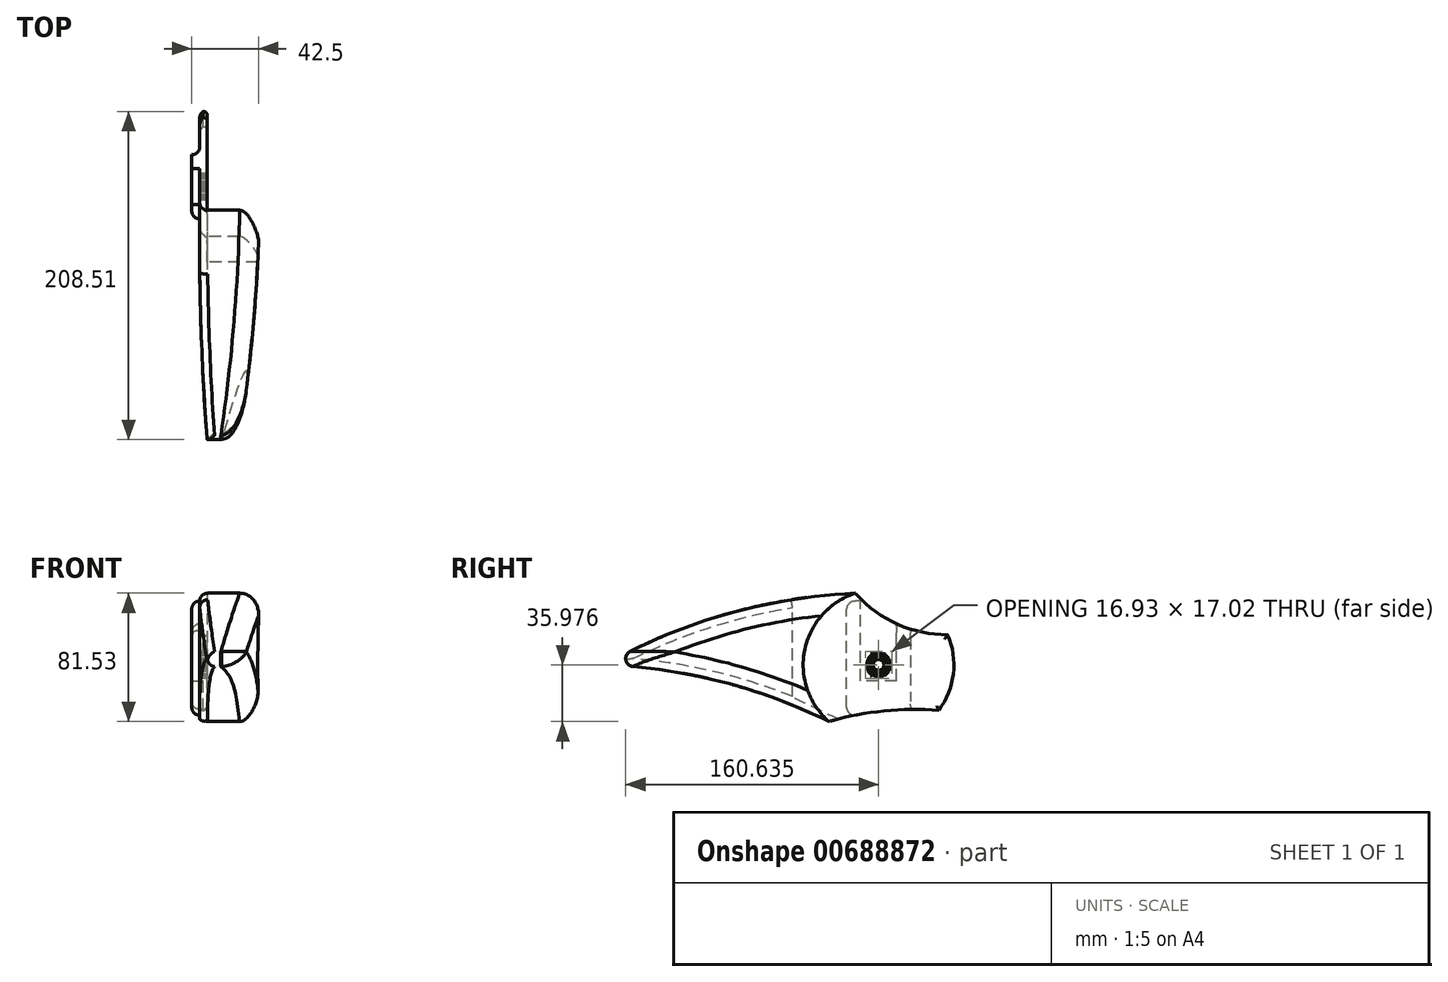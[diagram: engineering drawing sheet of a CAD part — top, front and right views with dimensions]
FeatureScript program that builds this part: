
annotation { "Feature Type Name" : "Feature", "Feature Type Description" : "" }
export const myFeature = defineFeature(function(context is Context, id is Id, definition is map)
    precondition{}
    {
        {
            var Q0;
            Q0=qCreatedBy(makeId("Right.planeOp"),FACE);
            var sketch = newSketch(context, id + "F0", { "sketchPlane" : qUnion([Q0])});
            skArc(sketch, "E0.0", {"start": v(-15.25, 45.51) * mm, "mid": v(-47.42, 9.65) * mm, "end": v(-32.12, -36.02) * mm});
            skArc(sketch, "E1", {"start": v(-15.25, 45.51) * mm, "mid": v(-97.5, 32.14) * mm, "end": v(-174.4, 0) * mm});
            skArc(sketch, "E2", {"start": v(-32.12, -36.02) * mm, "mid": v(-101.34, -10.43) * mm, "end": v(-174.4, 0) * mm});
            skArc(sketch, "E3", {"start": v(37.7, -28.86) * mm, "mid": v(2.47, -29.33) * mm, "end": v(-32.12, -36.02) * mm});
            skArc(sketch, "E4", {"start": v(-15.25, 45.51) * mm, "mid": v(11.16, 25.94) * mm, "end": v(43.33, 19.14) * mm});
            skArc(sketch, "E5.trimOffspring", {"start": v(37.7, -28.86) * mm, "mid": v(47.01, -5.62) * mm, "end": v(43.33, 19.14) * mm});
            skCircle(sketch, "E6", {"center": v(-0.54, -0.04) * mm, "radius": 3.43 * mm});
            skLineSegment(sketch, "E7", {"start": v(-0.54, -0.04) * mm, "end": v(-0.54, 10.9) * mm, "construction": true});
            skLineSegment(sketch, "E8.bottom", {"start": v(-0.55, 3.38) * mm, "end": v(-0.52, 3.38) * mm});
            skLineSegment(sketch, "E8.top", {"start": v(-0.55, 8.46) * mm, "end": v(-0.52, 8.46) * mm});
            skLineSegment(sketch, "E8.left", {"start": v(-0.55, 3.38) * mm, "end": v(-0.55, 8.46) * mm});
            skLineSegment(sketch, "E8.right", {"start": v(-0.52, 3.38) * mm, "end": v(-0.52, 8.46) * mm});
            skLineSegment(sketch, "E9.1.0", {"start": v(-1.24, 3.31) * mm, "end": v(-2.3, 8.28) * mm});
            skLineSegment(sketch, "E9.1.1", {"start": v(-1.26, 3.3) * mm, "end": v(-2.32, 8.28) * mm});
            skLineSegment(sketch, "E9.1.2", {"start": v(-2.32, 8.28) * mm, "end": v(-2.3, 8.28) * mm});
            skLineSegment(sketch, "E9.1.3", {"start": v(-1.26, 3.3) * mm, "end": v(-1.24, 3.31) * mm});
            skLineSegment(sketch, "E9.2.0", {"start": v(-1.92, 3.1) * mm, "end": v(-3.98, 7.73) * mm});
            skLineSegment(sketch, "E9.2.1", {"start": v(-1.94, 3.08) * mm, "end": v(-4, 7.72) * mm});
            skLineSegment(sketch, "E9.2.2", {"start": v(-4, 7.72) * mm, "end": v(-3.98, 7.73) * mm});
            skLineSegment(sketch, "E9.2.3", {"start": v(-1.94, 3.08) * mm, "end": v(-1.92, 3.1) * mm});
            skLineSegment(sketch, "E9.3.0", {"start": v(-2.54, 2.74) * mm, "end": v(-5.53, 6.85) * mm});
            skLineSegment(sketch, "E9.3.1", {"start": v(-2.56, 2.72) * mm, "end": v(-5.55, 6.83) * mm});
            skLineSegment(sketch, "E9.3.2", {"start": v(-5.55, 6.83) * mm, "end": v(-5.53, 6.85) * mm});
            skLineSegment(sketch, "E9.3.3", {"start": v(-2.56, 2.72) * mm, "end": v(-2.54, 2.74) * mm});
            skLineSegment(sketch, "E9.4.0", {"start": v(-3.08, 2.26) * mm, "end": v(-6.85, 5.66) * mm});
            skLineSegment(sketch, "E9.4.1", {"start": v(-3.1, 2.24) * mm, "end": v(-6.87, 5.64) * mm});
            skLineSegment(sketch, "E9.4.2", {"start": v(-6.87, 5.64) * mm, "end": v(-6.85, 5.66) * mm});
            skLineSegment(sketch, "E9.4.3", {"start": v(-3.1, 2.24) * mm, "end": v(-3.08, 2.26) * mm});
            skLineSegment(sketch, "E9.5.0", {"start": v(-3.5, 1.68) * mm, "end": v(-7.9, 4.22) * mm});
            skLineSegment(sketch, "E9.5.1", {"start": v(-3.51, 1.66) * mm, "end": v(-7.91, 4.2) * mm});
            skLineSegment(sketch, "E9.5.2", {"start": v(-7.91, 4.2) * mm, "end": v(-7.9, 4.22) * mm});
            skLineSegment(sketch, "E9.5.3", {"start": v(-3.51, 1.66) * mm, "end": v(-3.5, 1.68) * mm});
            skLineSegment(sketch, "E9.6.0", {"start": v(-3.8, 1.03) * mm, "end": v(-8.62, 2.6) * mm});
            skLineSegment(sketch, "E9.6.1", {"start": v(-3.8, 1) * mm, "end": v(-8.63, 2.57) * mm});
            skLineSegment(sketch, "E9.6.2", {"start": v(-8.63, 2.57) * mm, "end": v(-8.62, 2.6) * mm});
            skLineSegment(sketch, "E9.6.3", {"start": v(-3.8, 1) * mm, "end": v(-3.8, 1.03) * mm});
            skLineSegment(sketch, "E9.7.0", {"start": v(-3.94, 0.33) * mm, "end": v(-9, 0.86) * mm});
            skLineSegment(sketch, "E9.7.1", {"start": v(-3.95, 0.3) * mm, "end": v(-9, 0.83) * mm});
            skLineSegment(sketch, "E9.7.2", {"start": v(-9, 0.83) * mm, "end": v(-9, 0.86) * mm});
            skLineSegment(sketch, "E9.7.3", {"start": v(-3.95, 0.3) * mm, "end": v(-3.94, 0.33) * mm});
            skLineSegment(sketch, "E9.8.0", {"start": v(-3.95, -0.39) * mm, "end": v(-9, -0.92) * mm});
            skLineSegment(sketch, "E9.8.1", {"start": v(-3.94, -0.42) * mm, "end": v(-9, -0.95) * mm});
            skLineSegment(sketch, "E9.8.2", {"start": v(-9, -0.95) * mm, "end": v(-9, -0.92) * mm});
            skLineSegment(sketch, "E9.8.3", {"start": v(-3.94, -0.42) * mm, "end": v(-3.95, -0.39) * mm});
            skLineSegment(sketch, "E9.9.0", {"start": v(-3.8, -1.1) * mm, "end": v(-8.63, -2.66) * mm});
            skLineSegment(sketch, "E9.9.1", {"start": v(-3.8, -1.12) * mm, "end": v(-8.62, -2.69) * mm});
            skLineSegment(sketch, "E9.9.2", {"start": v(-8.62, -2.69) * mm, "end": v(-8.63, -2.66) * mm});
            skLineSegment(sketch, "E9.9.3", {"start": v(-3.8, -1.12) * mm, "end": v(-3.8, -1.1) * mm});
            skLineSegment(sketch, "E10.3.10.0", {"start": v(-3.5, -1.77) * mm, "end": v(-7.9, -4.3) * mm});
            skLineSegment(sketch, "E10.4.10.0", {"start": v(-3.51, -1.75) * mm, "end": v(-7.91, -4.29) * mm});
            skLineSegment(sketch, "E10.6.10.0", {"start": v(-7.9, -4.3) * mm, "end": v(-7.91, -4.29) * mm});
            skLineSegment(sketch, "E10.9.10.0", {"start": v(-3.5, -1.77) * mm, "end": v(-3.51, -1.75) * mm});
            skLineSegment(sketch, "E11.3.11.0", {"start": v(-3.08, -2.35) * mm, "end": v(-6.85, -5.75) * mm});
            skLineSegment(sketch, "E11.4.11.0", {"start": v(-3.1, -2.33) * mm, "end": v(-6.87, -5.73) * mm});
            skLineSegment(sketch, "E11.6.11.0", {"start": v(-6.85, -5.75) * mm, "end": v(-6.87, -5.73) * mm});
            skLineSegment(sketch, "E11.9.11.0", {"start": v(-3.08, -2.35) * mm, "end": v(-3.1, -2.33) * mm});
            skLineSegment(sketch, "E12.3.12.0", {"start": v(-2.54, -2.83) * mm, "end": v(-5.53, -6.94) * mm});
            skLineSegment(sketch, "E12.4.12.0", {"start": v(-2.56, -2.81) * mm, "end": v(-5.55, -6.92) * mm});
            skLineSegment(sketch, "E12.6.12.0", {"start": v(-5.53, -6.94) * mm, "end": v(-5.55, -6.92) * mm});
            skLineSegment(sketch, "E12.9.12.0", {"start": v(-2.54, -2.83) * mm, "end": v(-2.56, -2.81) * mm});
            skLineSegment(sketch, "E13.3.13.0", {"start": v(-1.92, -3.18) * mm, "end": v(-3.98, -7.82) * mm});
            skLineSegment(sketch, "E13.4.13.0", {"start": v(-1.94, -3.17) * mm, "end": v(-4, -7.81) * mm});
            skLineSegment(sketch, "E13.6.13.0", {"start": v(-3.98, -7.82) * mm, "end": v(-4, -7.81) * mm});
            skLineSegment(sketch, "E13.9.13.0", {"start": v(-1.92, -3.18) * mm, "end": v(-1.94, -3.17) * mm});
            skLineSegment(sketch, "E13.3.14.0", {"start": v(-1.24, -3.4) * mm, "end": v(-2.3, -8.37) * mm});
            skLineSegment(sketch, "E13.4.14.0", {"start": v(-1.26, -3.4) * mm, "end": v(-2.32, -8.36) * mm});
            skLineSegment(sketch, "E13.6.14.0", {"start": v(-2.3, -8.37) * mm, "end": v(-2.32, -8.36) * mm});
            skLineSegment(sketch, "E13.9.14.0", {"start": v(-1.24, -3.4) * mm, "end": v(-1.26, -3.4) * mm});
            skLineSegment(sketch, "E14.3.15.0", {"start": v(-0.52, -3.47) * mm, "end": v(-0.52, -8.55) * mm});
            skLineSegment(sketch, "E14.4.15.0", {"start": v(-0.55, -3.47) * mm, "end": v(-0.55, -8.55) * mm});
            skLineSegment(sketch, "E14.6.15.0", {"start": v(-0.52, -8.55) * mm, "end": v(-0.55, -8.55) * mm});
            skLineSegment(sketch, "E14.9.15.0", {"start": v(-0.52, -3.47) * mm, "end": v(-0.55, -3.47) * mm});
            skLineSegment(sketch, "E14.3.16.0", {"start": v(0.2, -3.4) * mm, "end": v(1.25, -8.36) * mm});
            skLineSegment(sketch, "E14.4.16.0", {"start": v(0.17, -3.4) * mm, "end": v(1.22, -8.37) * mm});
            skLineSegment(sketch, "E14.6.16.0", {"start": v(1.25, -8.36) * mm, "end": v(1.22, -8.37) * mm});
            skLineSegment(sketch, "E14.9.16.0", {"start": v(0.2, -3.4) * mm, "end": v(0.17, -3.4) * mm});
            skLineSegment(sketch, "E14.3.17.0", {"start": v(0.87, -3.17) * mm, "end": v(2.94, -7.81) * mm});
            skLineSegment(sketch, "E14.4.17.0", {"start": v(0.85, -3.18) * mm, "end": v(2.91, -7.82) * mm});
            skLineSegment(sketch, "E14.6.17.0", {"start": v(2.94, -7.81) * mm, "end": v(2.91, -7.82) * mm});
            skLineSegment(sketch, "E14.9.17.0", {"start": v(0.87, -3.17) * mm, "end": v(0.85, -3.18) * mm});
            skLineSegment(sketch, "E14.3.18.0", {"start": v(1.5, -2.81) * mm, "end": v(4.48, -6.92) * mm});
            skLineSegment(sketch, "E14.4.18.0", {"start": v(1.47, -2.83) * mm, "end": v(4.46, -6.94) * mm});
            skLineSegment(sketch, "E14.6.18.0", {"start": v(4.48, -6.92) * mm, "end": v(4.46, -6.94) * mm});
            skLineSegment(sketch, "E14.9.18.0", {"start": v(1.5, -2.81) * mm, "end": v(1.47, -2.83) * mm});
            skLineSegment(sketch, "E14.3.19.0", {"start": v(2.02, -2.33) * mm, "end": v(5.8, -5.73) * mm});
            skLineSegment(sketch, "E14.4.19.0", {"start": v(2, -2.35) * mm, "end": v(5.78, -5.75) * mm});
            skLineSegment(sketch, "E14.6.19.0", {"start": v(5.8, -5.73) * mm, "end": v(5.78, -5.75) * mm});
            skLineSegment(sketch, "E14.9.19.0", {"start": v(2.02, -2.33) * mm, "end": v(2, -2.35) * mm});
            skLineSegment(sketch, "E15.3.20.0", {"start": v(2.44, -1.75) * mm, "end": v(6.84, -4.29) * mm});
            skLineSegment(sketch, "E15.4.20.0", {"start": v(2.43, -1.77) * mm, "end": v(6.83, -4.3) * mm});
            skLineSegment(sketch, "E15.6.20.0", {"start": v(6.84, -4.29) * mm, "end": v(6.83, -4.3) * mm});
            skLineSegment(sketch, "E15.9.20.0", {"start": v(2.44, -1.75) * mm, "end": v(2.43, -1.77) * mm});
            skLineSegment(sketch, "E15.3.21.0", {"start": v(2.73, -1.1) * mm, "end": v(7.56, -2.66) * mm});
            skLineSegment(sketch, "E15.4.21.0", {"start": v(2.72, -1.12) * mm, "end": v(7.55, -2.69) * mm});
            skLineSegment(sketch, "E15.6.21.0", {"start": v(7.56, -2.66) * mm, "end": v(7.55, -2.69) * mm});
            skLineSegment(sketch, "E15.9.21.0", {"start": v(2.73, -1.1) * mm, "end": v(2.72, -1.12) * mm});
            skLineSegment(sketch, "E15.3.22.0", {"start": v(2.88, -0.39) * mm, "end": v(7.93, -0.92) * mm});
            skLineSegment(sketch, "E15.4.22.0", {"start": v(2.87, -0.42) * mm, "end": v(7.93, -0.95) * mm});
            skLineSegment(sketch, "E15.6.22.0", {"start": v(7.93, -0.92) * mm, "end": v(7.93, -0.95) * mm});
            skLineSegment(sketch, "E15.9.22.0", {"start": v(2.88, -0.39) * mm, "end": v(2.87, -0.42) * mm});
            skLineSegment(sketch, "E15.3.23.0", {"start": v(2.87, 0.33) * mm, "end": v(7.93, 0.86) * mm});
            skLineSegment(sketch, "E15.4.23.0", {"start": v(2.88, 0.3) * mm, "end": v(7.93, 0.83) * mm});
            skLineSegment(sketch, "E15.6.23.0", {"start": v(7.93, 0.86) * mm, "end": v(7.93, 0.83) * mm});
            skLineSegment(sketch, "E15.9.23.0", {"start": v(2.87, 0.33) * mm, "end": v(2.88, 0.3) * mm});
            skLineSegment(sketch, "E15.3.24.0", {"start": v(2.72, 1.03) * mm, "end": v(7.55, 2.6) * mm});
            skLineSegment(sketch, "E15.4.24.0", {"start": v(2.73, 1) * mm, "end": v(7.56, 2.57) * mm});
            skLineSegment(sketch, "E15.6.24.0", {"start": v(7.55, 2.6) * mm, "end": v(7.56, 2.57) * mm});
            skLineSegment(sketch, "E15.9.24.0", {"start": v(2.72, 1.03) * mm, "end": v(2.73, 1) * mm});
            skLineSegment(sketch, "E16.3.25.0", {"start": v(2.43, 1.68) * mm, "end": v(6.83, 4.22) * mm});
            skLineSegment(sketch, "E16.4.25.0", {"start": v(2.44, 1.66) * mm, "end": v(6.84, 4.2) * mm});
            skLineSegment(sketch, "E16.6.25.0", {"start": v(6.83, 4.22) * mm, "end": v(6.84, 4.2) * mm});
            skLineSegment(sketch, "E16.9.25.0", {"start": v(2.43, 1.68) * mm, "end": v(2.44, 1.66) * mm});
            skLineSegment(sketch, "E16.3.26.0", {"start": v(2, 2.26) * mm, "end": v(5.78, 5.66) * mm});
            skLineSegment(sketch, "E16.4.26.0", {"start": v(2.02, 2.24) * mm, "end": v(5.8, 5.64) * mm});
            skLineSegment(sketch, "E16.6.26.0", {"start": v(5.78, 5.66) * mm, "end": v(5.8, 5.64) * mm});
            skLineSegment(sketch, "E16.9.26.0", {"start": v(2, 2.26) * mm, "end": v(2.02, 2.24) * mm});
            skLineSegment(sketch, "E16.3.27.0", {"start": v(1.47, 2.74) * mm, "end": v(4.46, 6.85) * mm});
            skLineSegment(sketch, "E16.4.27.0", {"start": v(1.5, 2.72) * mm, "end": v(4.48, 6.83) * mm});
            skLineSegment(sketch, "E16.6.27.0", {"start": v(4.46, 6.85) * mm, "end": v(4.48, 6.83) * mm});
            skLineSegment(sketch, "E16.9.27.0", {"start": v(1.47, 2.74) * mm, "end": v(1.5, 2.72) * mm});
            skLineSegment(sketch, "E16.3.28.0", {"start": v(0.85, 3.1) * mm, "end": v(2.91, 7.73) * mm});
            skLineSegment(sketch, "E16.4.28.0", {"start": v(0.87, 3.08) * mm, "end": v(2.94, 7.72) * mm});
            skLineSegment(sketch, "E16.6.28.0", {"start": v(2.91, 7.73) * mm, "end": v(2.94, 7.72) * mm});
            skLineSegment(sketch, "E16.9.28.0", {"start": v(0.85, 3.1) * mm, "end": v(0.87, 3.08) * mm});
            skLineSegment(sketch, "E16.3.29.0", {"start": v(0.17, 3.31) * mm, "end": v(1.22, 8.28) * mm});
            skLineSegment(sketch, "E16.4.29.0", {"start": v(0.2, 3.3) * mm, "end": v(1.25, 8.28) * mm});
            skLineSegment(sketch, "E16.6.29.0", {"start": v(1.22, 8.28) * mm, "end": v(1.25, 8.28) * mm});
            skLineSegment(sketch, "E16.9.29.0", {"start": v(0.17, 3.31) * mm, "end": v(0.2, 3.3) * mm});
            skSolve(sketch);
        }
        {
            var Q0;
            Q0=makeQuery(id+"F0.imprint","IMPRINT",FACE,{"disambiguationData":[TD([[makeQuery(id+"F0.imprint","IMPRINT",EDGE,{"derivedFrom":sQuery(id+"F0.wireOp",EDGE,"E0.0")}),1.0]])]});
            extrude(context, id + "F1", {"entities" : qUnion([Q0]), "depth" : 4.83 * mm, "offsetDistance" : 25.4 * mm});
        }
        {
            var Q0;
            Q0=makeQuery(id+"F0.imprint","IMPRINT",FACE,{"disambiguationData":[TD([[makeQuery(id+"F0.imprint","IMPRINT",EDGE,{"derivedFrom":sQuery(id+"F0.wireOp",EDGE,"E0.0")}),-1.0]])]});
            extrude(context, id + "F2", {"entities" : qUnion([Q0]), "operationType" : NewBodyOperationType.ADD, "depth" : 38.1 * mm, "offsetDistance" : 25.4 * mm});
        }
        {
            var Q0;
            Q0=makeQuery(id+"F1.opExtrude","CAP_EDGE",EDGE,{"disambiguationData":[OSD([sQuery(id+"F0.wireOp",EDGE,"E4")])],"isStart":false});
            var Q1;
            Q1=makeQuery(id+"F1.opExtrude","CAP_EDGE",EDGE,{"disambiguationData":[OSD([sQuery(id+"F0.wireOp",EDGE,"E3")])],"isStart":false});
            var Q2;
            Q2=makeQuery(id+"F1.opExtrude","CAP_EDGE",EDGE,{"disambiguationData":[OSD([sQuery(id+"F0.wireOp",EDGE,"E5.trimOffspring")])],"isStart":false});
            fillet(context, id + "F3", {"entities" : qUnion([Q0, Q1, Q2]), "radius" : 2.54 * mm, "tangentPropagation" : true, "allowEdgeOverflow" : false});
        }
        {
            var Q0;
            Q0=makeQuery(id+"F2.boolean.opBoolean","SPLIT",EDGE,{"derivedFrom":makeQuery(id+"F2.opExtrude","SWEPT_EDGE",EDGE,{"disambiguationData":[OSD([sQuery(id+"F0.wireOp",EDGE,"E0.0"),sQuery(id+"F0.wireOp",EDGE,"E1"),sQuery(id+"F0.wireOp",EDGE,"E4")])]})});
            cPlane(context, id + "F4", {"entities" : qUnion([Q0]), "cplaneType" : CPlaneType.LINE_ANGLE, "offset" : 0 * mm, "angle" : 90 * degree, "width" : 152.4 * mm, "height" : 152.4 * mm});
        }
        {
            var Q0;
            Q0=qCreatedBy(id+"F4.planeOp",FACE);
            var sketch = newSketch(context, id + "F5", { "sketchPlane" : qUnion([Q0])});
            skLineSegment(sketch, "E17", {"start": v(22.21, -178.45) * mm, "end": v(43.85, -178.45) * mm});
            skLineSegment(sketch, "E18", {"start": v(43.85, -178.45) * mm, "end": v(43.85, -15.25) * mm});
            skLineSegment(sketch, "E19", {"start": v(43.85, -15.25) * mm, "end": v(38.1, -15.25) * mm});
            skArc(sketch, "E20", {"start": v(22.21, -178.45) * mm, "mid": v(33.2, -97.15) * mm, "end": v(38.1, -15.25) * mm});
            skArc(sketch, "E21", {"start": v(0, -15.25) * mm, "mid": v(0.95, -94.53) * mm, "end": v(5.71, -173.68) * mm});
            skLineSegment(sketch, "E22", {"start": v(0, -15.25) * mm, "end": v(-6.93, -15.25) * mm});
            skLineSegment(sketch, "E23", {"start": v(-6.93, -15.25) * mm, "end": v(-6.93, -180.22) * mm});
            skLineSegment(sketch, "E24", {"start": v(-6.93, -180.22) * mm, "end": v(5.71, -180.22) * mm});
            skLineSegment(sketch, "E25", {"start": v(5.71, -180.22) * mm, "end": v(5.71, -173.68) * mm});
            skSolve(sketch);
        }
        {
            var Q0;
            Q0 = qSketchRegion(id + "F5", true);
            extrude(context, id + "F6", {"entities" : qUnion([Q0]), "operationType" : NewBodyOperationType.REMOVE, "endBound" : BoundingType.THROUGH_ALL, "oppositeDirection" : true, "depth" : 25.4 * mm, "offsetDistance" : 25.4 * mm});
        }
        {
            var Q0;
            Q0=makeQuery(id+"F6.boolean.opBoolean","INTERSECT",EDGE,{"derivedFrom":[makeQuery(id+"F2.opExtrude","SWEPT_FACE",FACE,{"disambiguationData":[OSD([sQuery(id+"F0.wireOp",EDGE,"E1")])]}),makeQuery(id+"F6.opExtrude","SWEPT_FACE",FACE,{"disambiguationData":[OSD([sQuery(id+"F5.wireOp",EDGE,"E20")])]})]});
            var Q1;
            Q1=makeQuery(id+"F6.boolean.opBoolean","INTERSECT",EDGE,{"derivedFrom":[makeQuery(id+"F2.opExtrude","SWEPT_FACE",FACE,{"disambiguationData":[OSD([sQuery(id+"F0.wireOp",EDGE,"E2")])]}),makeQuery(id+"F6.opExtrude","SWEPT_FACE",FACE,{"disambiguationData":[OSD([sQuery(id+"F5.wireOp",EDGE,"E20")])]})]});
            fillet(context, id + "F7", {"entities" : qUnion([Q0, Q1]), "radius" : 12.7 * mm, "tangentPropagation" : true, "allowEdgeOverflow" : false});
        }
        {
            var Q0;
            Q0=makeQuery(id+"F2.opExtrude","SWEPT_EDGE",EDGE,{"disambiguationData":[OSD([sQuery(id+"F0.wireOp",EDGE,"E1"),sQuery(id+"F0.wireOp",EDGE,"E2")])]});
            var Q1;
            Q1=makeQuery(id+"F6.boolean.opBoolean","INTERSECT",EDGE,{"derivedFrom":[makeQuery(id+"F2.opExtrude","SWEPT_FACE",FACE,{"disambiguationData":[OSD([sQuery(id+"F0.wireOp",EDGE,"E1")])]}),makeQuery(id+"F6.opExtrude","SWEPT_FACE",FACE,{"disambiguationData":[OSD([sQuery(id+"F5.wireOp",EDGE,"E21")])]})]});
            var Q2;
            Q2=makeQuery(id+"F6.boolean.opBoolean","INTERSECT",EDGE,{"derivedFrom":[makeQuery(id+"F2.opExtrude","SWEPT_FACE",FACE,{"disambiguationData":[OSD([sQuery(id+"F0.wireOp",EDGE,"E2")])]}),makeQuery(id+"F6.opExtrude","SWEPT_FACE",FACE,{"disambiguationData":[OSD([sQuery(id+"F5.wireOp",EDGE,"E21")])]})]});
            fillet(context, id + "F8", {"entities" : qUnion([Q0, Q1, Q2]), "radius" : 5.08 * mm, "tangentPropagation" : true, "allowEdgeOverflow" : false});
        }
        {
            var Q0;
            Q0=makeQuery(id+"F0.imprint","IMPRINT",FACE,{"disambiguationData":[TD([[makeQuery(id+"F0.imprint","IMPRINT",EDGE,{"derivedFrom":sQuery(id+"F0.wireOp",EDGE,"E0.0")}),1.0]])]});
            var sketch = newSketch(context, id + "F9", { "sketchPlane" : qUnion([Q0])});
            skCircle(sketch, "E26.0", {"center": v(-0.54, -0.04) * mm, "radius": 3.43 * mm});
            skArc(sketch, "E27.0", {"start": v(-15.25, 45.51) * mm, "mid": v(11.16, 25.94) * mm, "end": v(43.33, 19.14) * mm});
            skArc(sketch, "E28.0", {"start": v(37.7, -28.86) * mm, "mid": v(2.47, -29.33) * mm, "end": v(-32.12, -36.02) * mm});
            skLineSegment(sketch, "E29", {"start": v(19.78, 22.66) * mm, "end": v(19.78, -28.32) * mm});
            skArc(sketch, "E30.0", {"start": v(-55.2, 36.35) * mm, "mid": v(-32.95, 39.2) * mm, "end": v(-10.56, 40.6) * mm});
            skLineSegment(sketch, "E31", {"start": v(-20.86, -33.14) * mm, "end": v(-20.86, 40.13) * mm});
            skLineSegment(sketch, "E32.bottom", {"start": v(10.9, -10.2) * mm, "end": v(-11.97, -10.2) * mm});
            skLineSegment(sketch, "E32.top", {"start": v(10.9, 42.4) * mm, "end": v(-11.97, 42.4) * mm});
            skLineSegment(sketch, "E32.left", {"start": v(10.9, -10.2) * mm, "end": v(10.9, 42.4) * mm});
            skLineSegment(sketch, "E32.right", {"start": v(-11.97, -10.2) * mm, "end": v(-11.97, 42.4) * mm});
            skSolve(sketch);
        }
        {
            var Q0;
            {var subQ4=sQuery(id+"F9.wireOp",EDGE,"E29");Q0=makeQuery(id+"F9.imprint","IMPRINT",FACE,{"disambiguationData":[TD([[makeQuery(id+"F9.imprint","IMPRINT",EDGE,{"derivedFrom":subQ4}),-1.0]])]});}
            extrude(context, id + "F10", {"entities" : qUnion([Q0]), "operationType" : NewBodyOperationType.ADD, "oppositeDirection" : true, "depth" : 5.08 * mm, "offsetDistance" : 25.4 * mm});
        }
        {
            var Q0;
            Q0=makeQuery(id+"F10.opExtrude","CAP_EDGE",EDGE,{"disambiguationData":[OSD([sQuery(id+"F9.wireOp",EDGE,"E29")])],"isStart":true});
            var Q1;
            Q1=makeQuery(id+"F10.opExtrude","CAP_EDGE",EDGE,{"disambiguationData":[OSD([sQuery(id+"F9.wireOp",EDGE,"E31")])],"isStart":false});
            fillet(context, id + "F11", {"entities" : qUnion([Q0, Q1]), "radius" : 5.08 * mm, "tangentPropagation" : true, "allowEdgeOverflow" : false});
        }
        {
            var Q0;
            Q0=makeQuery(id+"F1.opExtrude","CAP_EDGE",EDGE,{"disambiguationData":[OSD([sQuery(id+"F0.wireOp",EDGE,"E5.trimOffspring")])],"isStart":true});
            var Q1;
            Q1=makeQuery(id+"F10.opExtrude","CAP_EDGE",EDGE,{"disambiguationData":[OSD([sQuery(id+"F9.wireOp",EDGE,"E28.0")])],"isStart":false});
            var Q2;
            Q2=makeQuery(id+"F10.opExtrude","CAP_EDGE",EDGE,{"disambiguationData":[OSD([sQuery(id+"F9.wireOp",EDGE,"E27.0")])],"isStart":false});
            var Q3;
            Q3=makeQuery(id+"F10.opExtrude","CAP_EDGE",EDGE,{"disambiguationData":[OSD([sQuery(id+"F9.wireOp",EDGE,"E30.0")])],"isStart":false});
            fillet(context, id + "F12", {"entities" : qUnion([Q0, Q1, Q2, Q3]), "radius" : 5.08 * mm, "tangentPropagation" : true, "allowEdgeOverflow" : false});
        }
    });
